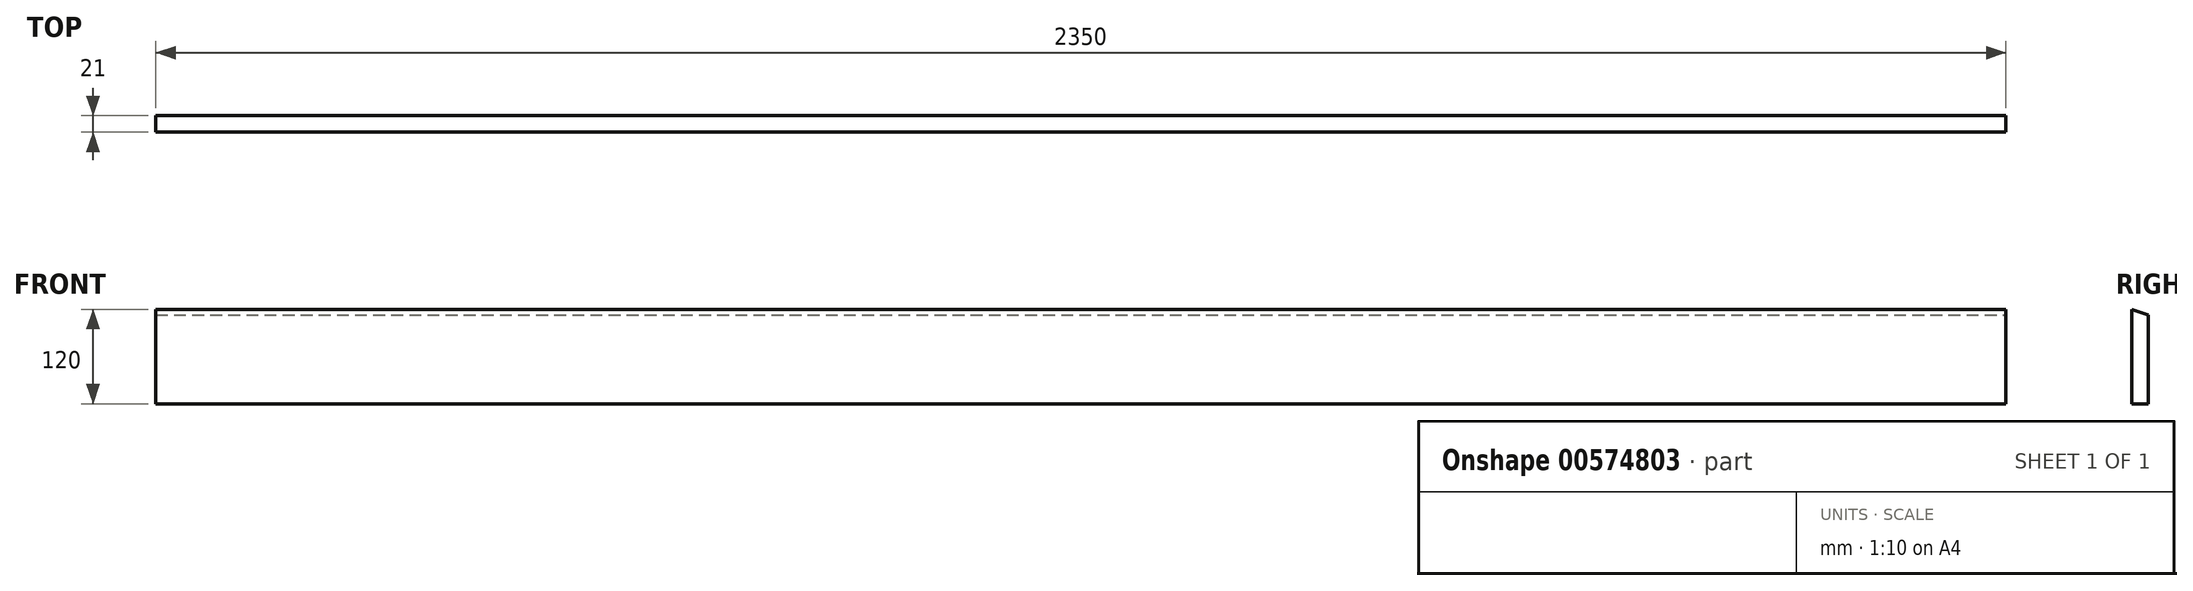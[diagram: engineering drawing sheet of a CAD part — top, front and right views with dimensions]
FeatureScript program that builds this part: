
annotation { "Feature Type Name" : "Feature", "Feature Type Description" : "" }
export const myFeature = defineFeature(function(context is Context, id is Id, definition is map)
    precondition{}
    {
        {
            var Q0;
            Q0=qCreatedBy(makeId("Right.planeOp"),FACE);
            var sketch = newSketch(context, id + "F0", { "sketchPlane" : qUnion([Q0])});
            skLineSegment(sketch, "E0.bottom", {"start": v(-10.5, 60) * mm, "end": v(10.5, 60) * mm});
            skLineSegment(sketch, "E0.top", {"start": v(-10.5, -60) * mm, "end": v(10.5, -60) * mm});
            skLineSegment(sketch, "E0.left", {"start": v(-10.5, 60) * mm, "end": v(-10.5, -60) * mm});
            skLineSegment(sketch, "E0.right", {"start": v(10.5, 60) * mm, "end": v(10.5, -60) * mm});
            skSolve(sketch);
        }
        {
            var Q0;
            Q0 = qSketchRegion(id + "F0", true);
            extrude(context, id + "F1", {"entities" : qUnion([Q0]), "depth" : 2350 * mm, "offsetDistance" : 25 * mm});
        }
        {
            var Q0;
            Q0=makeQuery(id+"F1.opExtrude","CAP_FACE",FACE,{"disambiguationData":[OSD([sQuery(id+"F0.wireOp",EDGE,"E0.bottom"),sQuery(id+"F0.wireOp",EDGE,"E0.top"),sQuery(id+"F0.wireOp",EDGE,"E0.left"),sQuery(id+"F0.wireOp",EDGE,"E0.right")])],"isStart":false});
            var sketch = newSketch(context, id + "F2", { "sketchPlane" : qUnion([Q0])});
            skLineSegment(sketch, "E1", {"start": v(-10.5, 60) * mm, "end": v(10.5, 60) * mm});
            skLineSegment(sketch, "E2", {"start": v(10.5, 60) * mm, "end": v(10.5, 53) * mm});
            skLineSegment(sketch, "E3", {"start": v(10.5, 53) * mm, "end": v(-10.5, 60) * mm});
            skSolve(sketch);
        }
        {
            var Q0;
            Q0=makeQuery(id+"F2.imprint","IMPRINT",FACE,{"disambiguationData":[TD([[makeQuery(id+"F2.imprint","IMPRINT",EDGE,{"derivedFrom":sQuery(id+"F2.wireOp",EDGE,"E1")}),-1.0]])]});
            extrude(context, id + "F3", {"entities" : qUnion([Q0]), "operationType" : NewBodyOperationType.REMOVE, "endBound" : BoundingType.THROUGH_ALL, "oppositeDirection" : true, "depth" : 25 * mm, "offsetDistance" : 25 * mm});
        }
    });
